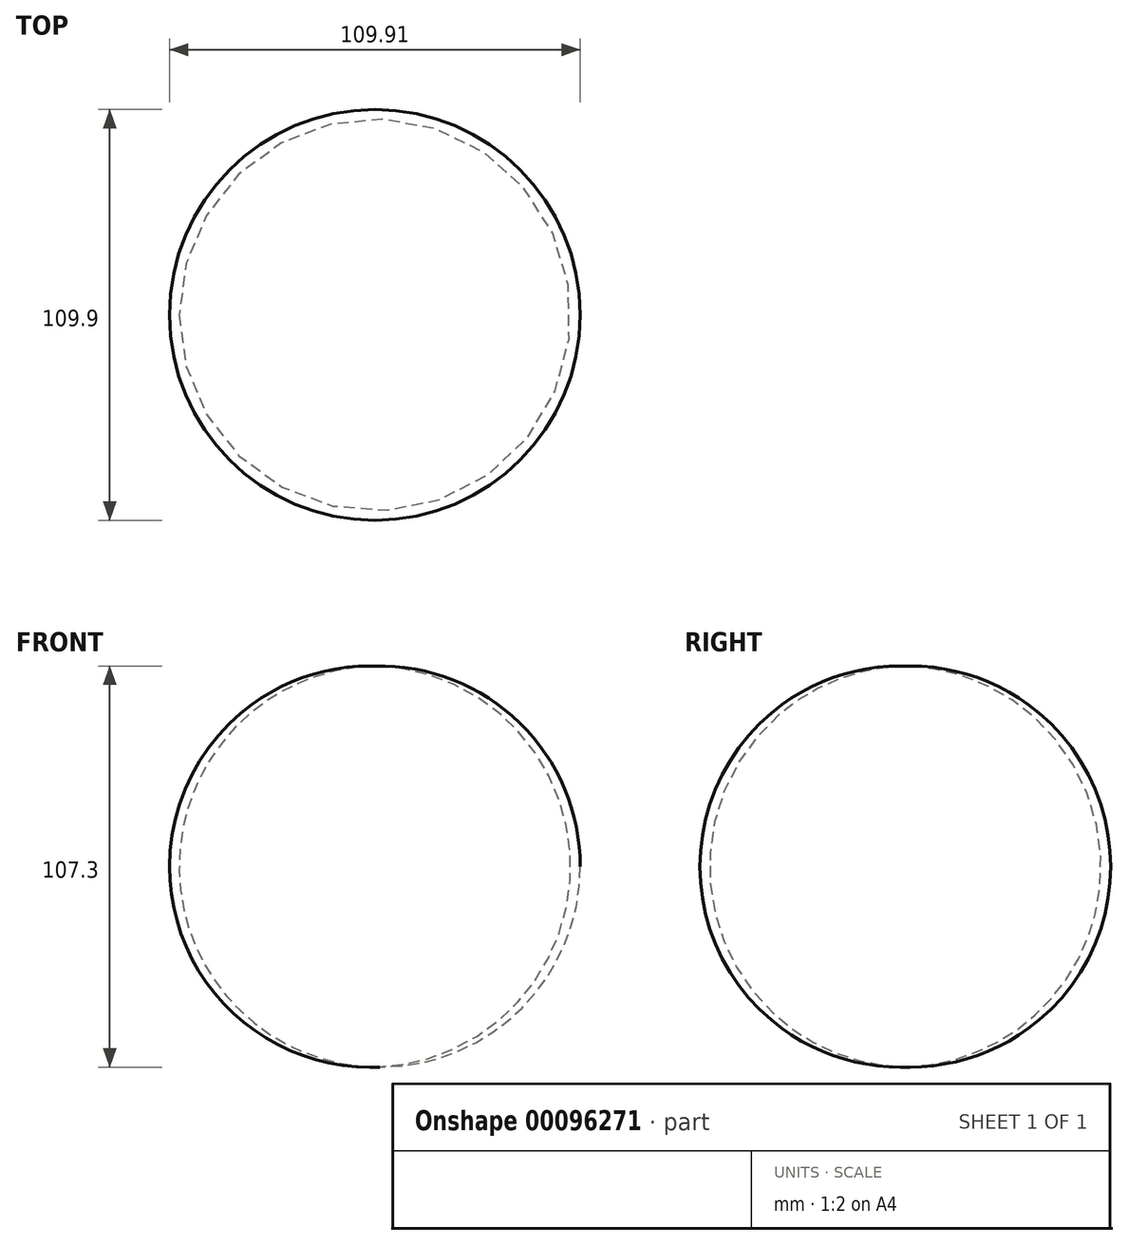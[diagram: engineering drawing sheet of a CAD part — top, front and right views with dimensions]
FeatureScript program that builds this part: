
annotation { "Feature Type Name" : "Feature", "Feature Type Description" : "" }
export const myFeature = defineFeature(function(context is Context, id is Id, definition is map)
    precondition{}
    {
        {
            var Q0;
            Q0=qCreatedBy(makeId("Front.planeOp"),FACE);
            var sketch = newSketch(context, id + "F0", { "sketchPlane" : qUnion([Q0])});
            skLineSegment(sketch, "E0", {"start": v(-50.96, 59.45) * mm, "end": v(-50.96, -47.83) * mm});
            skArc(sketch, "E1", {"start": v(-50.96, -47.83) * mm, "mid": v(1.4, 5.81) * mm, "end": v(-50.96, 59.45) * mm});
            skSolve(sketch);
        }
        {
            var Q0;
            Q0=makeQuery(id+"F0.imprint","IMPRINT",FACE,{"disambiguationData":[TD([[makeQuery(id+"F0.imprint","IMPRINT",EDGE,{"derivedFrom":sQuery(id+"F0.wireOp",EDGE,"E0")}),1.0]])]});
            var Q1;
            Q1=sQuery(id+"F0.wireOp",EDGE,"E0");
            revolve(context, id + "F1", {"entities" : qUnion([Q0]), "axis" : qUnion([Q1]), "revolveType" : RevolveType.FULL});
        }
    });
